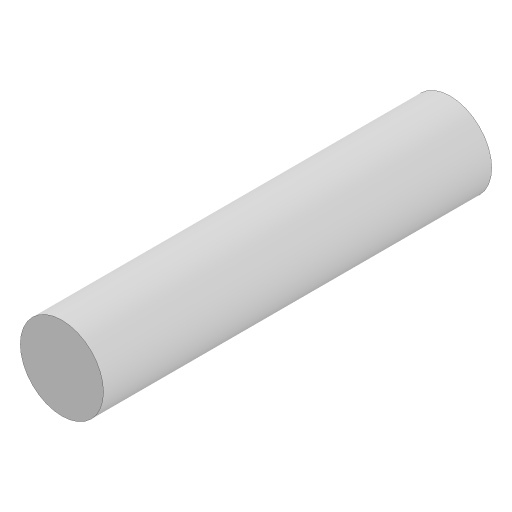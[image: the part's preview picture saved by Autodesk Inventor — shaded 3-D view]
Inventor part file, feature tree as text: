
AUTODESK INVENTOR PART (.ipt)
format: ipt  version: 2023 (Build 270158000, 158)  size: 87,040 bytes
history: native  units: mm
features: extrude x1, sketch x1
ambient origin geometry x8: Origin, YZ Plane, XZ Plane, XY Plane, X Axis, Y Axis, Z Axis, Center Point
bodies: Solid1 (feature_tree)
feature tree (2):
  extrude  "Extrusion1"  Depth=21.0mm TaperAngle=0.0deg
  sketch  "Sketch1"  dims[d0=4.5mm d1=21.0mm d2=0.0mm]
